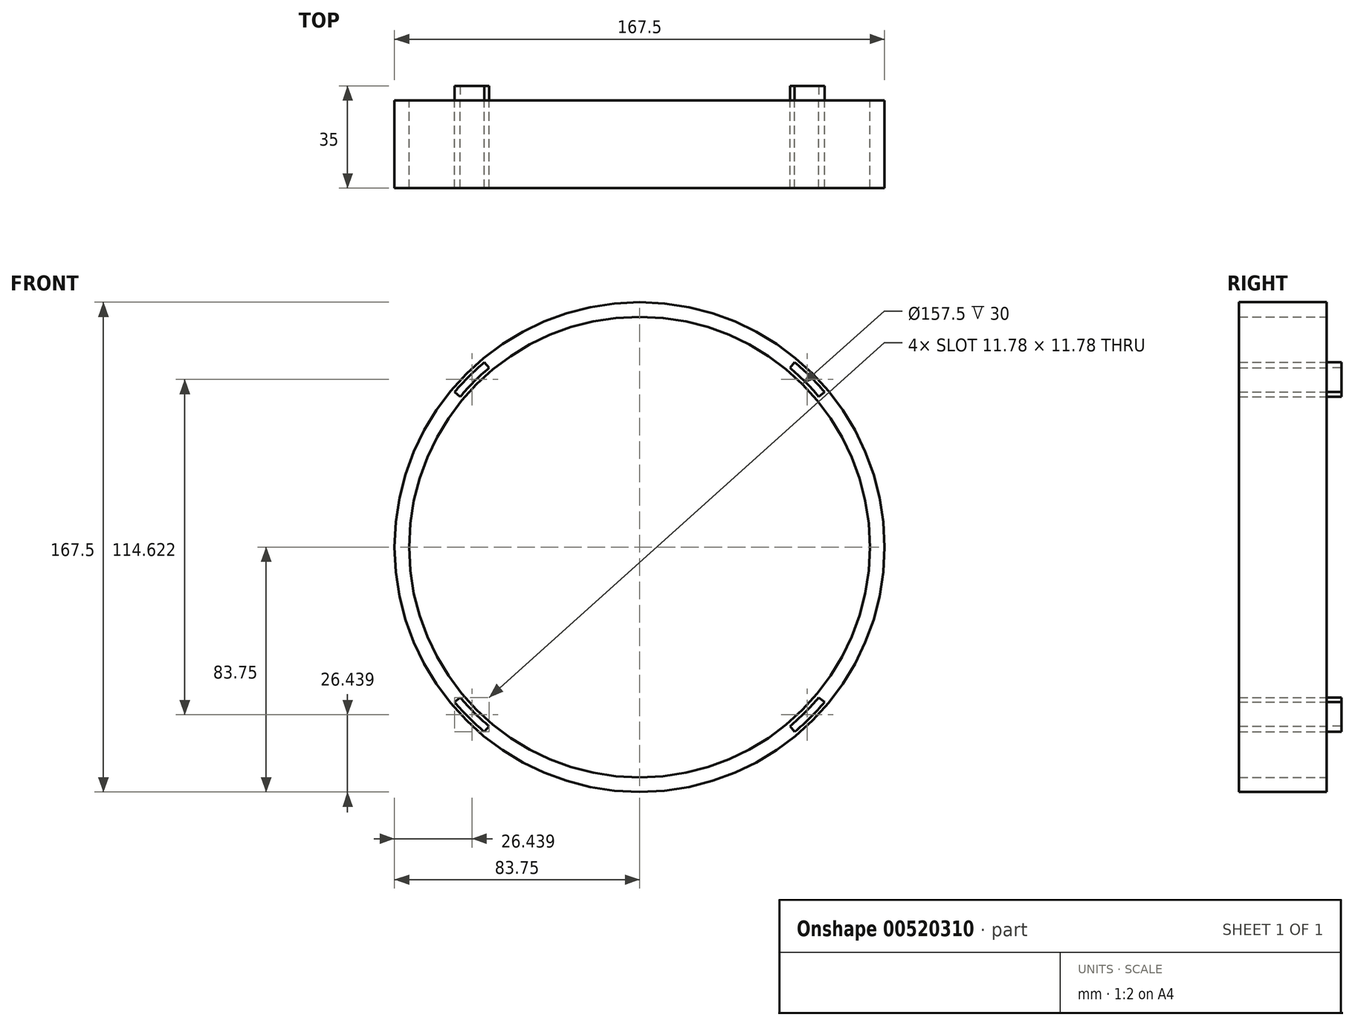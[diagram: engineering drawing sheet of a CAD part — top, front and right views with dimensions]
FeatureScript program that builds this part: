
annotation { "Feature Type Name" : "Feature", "Feature Type Description" : "" }
export const myFeature = defineFeature(function(context is Context, id is Id, definition is map)
    precondition{}
    {
        {
            var Q0;
            Q0=qCreatedBy(makeId("Front.planeOp"),FACE);
            var sketch = newSketch(context, id + "F0", { "sketchPlane" : qUnion([Q0])});
            skCircle(sketch, "E0", {"center": v(0, 0) * mm, "radius": 78.75 * mm});
            skCircle(sketch, "E1", {"center": v(0, 0) * mm, "radius": 83.75 * mm});
            skLineSegment(sketch, "E2", {"start": v(51.42, -61.28) * mm, "end": v(53.03, -63.2) * mm});
            skLineSegment(sketch, "E3", {"start": v(63.2, -53.03) * mm, "end": v(61.28, -51.42) * mm});
            skArc(sketch, "E4", {"start": v(51.42, -61.28) * mm, "mid": v(56.57, -56.57) * mm, "end": v(61.28, -51.42) * mm});
            skArc(sketch, "E5", {"start": v(53.03, -63.2) * mm, "mid": v(58.34, -58.34) * mm, "end": v(63.2, -53.03) * mm});
            skLineSegment(sketch, "E6", {"start": v(-63.2, -53.03) * mm, "end": v(-61.28, -51.42) * mm});
            skLineSegment(sketch, "E7", {"start": v(-53.03, -63.2) * mm, "end": v(-51.42, -61.28) * mm});
            skArc(sketch, "E8", {"start": v(-61.28, -51.42) * mm, "mid": v(-56.57, -56.57) * mm, "end": v(-51.42, -61.28) * mm});
            skArc(sketch, "E9", {"start": v(-63.2, -53.03) * mm, "mid": v(-58.34, -58.34) * mm, "end": v(-53.03, -63.2) * mm});
            skLineSegment(sketch, "E10", {"start": v(-53.03, 63.2) * mm, "end": v(-51.42, 61.28) * mm});
            skLineSegment(sketch, "E11", {"start": v(-63.2, 53.03) * mm, "end": v(-61.28, 51.42) * mm});
            skArc(sketch, "E12", {"start": v(-61.28, 51.42) * mm, "mid": v(-56.57, 56.57) * mm, "end": v(-51.42, 61.28) * mm});
            skArc(sketch, "E13", {"start": v(-63.2, 53.03) * mm, "mid": v(-58.34, 58.34) * mm, "end": v(-53.03, 63.2) * mm});
            skLineSegment(sketch, "E14", {"start": v(63.2, 53.03) * mm, "end": v(61.28, 51.42) * mm});
            skLineSegment(sketch, "E15", {"start": v(53.03, 63.2) * mm, "end": v(51.42, 61.28) * mm});
            skArc(sketch, "E16", {"start": v(51.42, 61.28) * mm, "mid": v(56.57, 56.57) * mm, "end": v(61.28, 51.42) * mm});
            skArc(sketch, "E17", {"start": v(63.2, 53.03) * mm, "mid": v(58.34, 58.34) * mm, "end": v(53.03, 63.2) * mm});
            skSolve(sketch);
        }
        {
            var Q0;
            Q0 = qSketchRegion(id + "F0", true);
            extrude(context, id + "F1", {"entities" : qUnion([Q0]), "depth" : 30 * mm, "offsetDistance" : 25 * mm});
        }
        {
            var Q0;
            Q0=makeQuery(id+"F0.imprint","IMPRINT",FACE,{"disambiguationData":[TD([[makeQuery(id+"F0.imprint","IMPRINT",EDGE,{"derivedFrom":sQuery(id+"F0.wireOp",EDGE,"E10")}),-1.0]])]});
            var Q1;
            Q1=makeQuery(id+"F0.imprint","IMPRINT",FACE,{"disambiguationData":[TD([[makeQuery(id+"F0.imprint","IMPRINT",EDGE,{"derivedFrom":sQuery(id+"F0.wireOp",EDGE,"E6")}),-1.0]])]});
            var Q2;
            Q2=makeQuery(id+"F0.imprint","IMPRINT",FACE,{"disambiguationData":[TD([[makeQuery(id+"F0.imprint","IMPRINT",EDGE,{"derivedFrom":sQuery(id+"F0.wireOp",EDGE,"E14")}),-1.0]])]});
            var Q3;
            Q3=makeQuery(id+"F0.imprint","IMPRINT",FACE,{"disambiguationData":[TD([[makeQuery(id+"F0.imprint","IMPRINT",EDGE,{"derivedFrom":sQuery(id+"F0.wireOp",EDGE,"E2")}),1.0]])]});
            extrude(context, id + "F2", {"entities" : qUnion([Q0, Q1, Q2, Q3]), "oppositeDirection" : true, "depth" : 5 * mm, "offsetDistance" : 25 * mm});
        }
        {
            var Q0;
            Q0=makeQuery(id+"F0.imprint","IMPRINT",FACE,{"disambiguationData":[TD([[makeQuery(id+"F0.imprint","IMPRINT",EDGE,{"derivedFrom":sQuery(id+"F0.wireOp",EDGE,"E10")}),-1.0]])]});
            var Q1;
            Q1=makeQuery(id+"F0.imprint","IMPRINT",FACE,{"disambiguationData":[TD([[makeQuery(id+"F0.imprint","IMPRINT",EDGE,{"derivedFrom":sQuery(id+"F0.wireOp",EDGE,"E6")}),-1.0]])]});
            var Q2;
            Q2=makeQuery(id+"F0.imprint","IMPRINT",FACE,{"disambiguationData":[TD([[makeQuery(id+"F0.imprint","IMPRINT",EDGE,{"derivedFrom":sQuery(id+"F0.wireOp",EDGE,"E2")}),1.0]])]});
            var Q3;
            Q3=makeQuery(id+"F0.imprint","IMPRINT",FACE,{"disambiguationData":[TD([[makeQuery(id+"F0.imprint","IMPRINT",EDGE,{"derivedFrom":sQuery(id+"F0.wireOp",EDGE,"E14")}),-1.0]])]});
            extrude(context, id + "F3", {"entities" : qUnion([Q0, Q1, Q2, Q3]), "depth" : 30 * mm, "offsetDistance" : 25 * mm});
        }
    });
